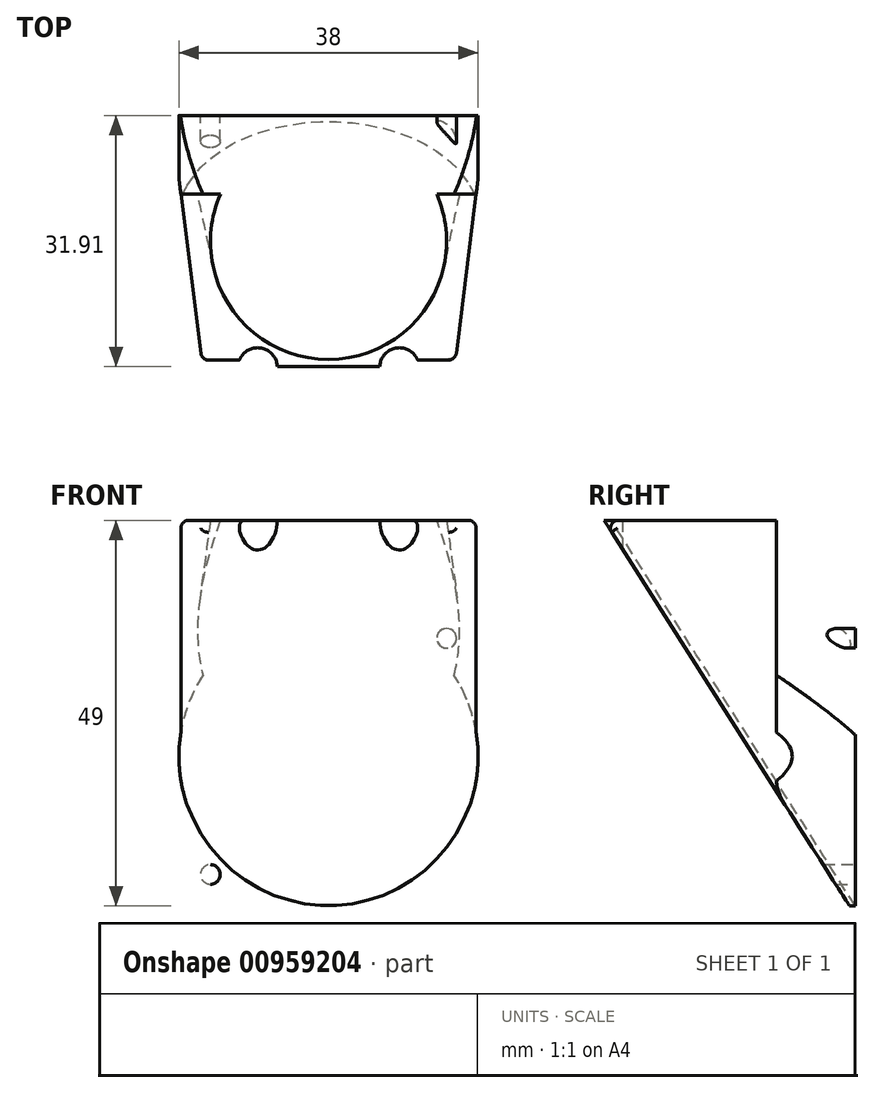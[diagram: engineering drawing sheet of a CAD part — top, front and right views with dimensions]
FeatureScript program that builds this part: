
annotation { "Feature Type Name" : "Feature", "Feature Type Description" : "" }
export const myFeature = defineFeature(function(context is Context, id is Id, definition is map)
    precondition{}
    {
        {
            var Q0;
            Q0=qCreatedBy(makeId("Top.planeOp"),FACE);
            var sketch = newSketch(context, id + "F0", { "sketchPlane" : qUnion([Q0])});
            skLineSegment(sketch, "E0.bottom", {"start": v(16, -16) * mm, "end": v(-16, -16) * mm});
            skPoint(sketch, "E0.middle", {"position": v(0, 0) * mm});
            skLineSegment(sketch, "E1", {"start": v(-20, 20.39) * mm, "end": v(-20, 8.27) * mm, "construction": true});
            skLineSegment(sketch, "E2", {"start": v(20, 19.24) * mm, "end": v(20, 5.53) * mm, "construction": true});
            skLineSegment(sketch, "E3", {"start": v(-16, 16) * mm, "end": v(-20, 16) * mm, "construction": true});
            skLineSegment(sketch, "E4", {"start": v(16, 16) * mm, "end": v(20, 16) * mm, "construction": true});
            skLineSegment(sketch, "E5", {"start": v(-16, -16) * mm, "end": v(-20, 16) * mm});
            skLineSegment(sketch, "E6", {"start": v(16, -16) * mm, "end": v(20, 16) * mm});
            skLineSegment(sketch, "E7", {"start": v(-20, 16) * mm, "end": v(20, 16) * mm});
            skCircle(sketch, "E8", {"center": v(-9, -16) * mm, "radius": 2.5 * mm});
            skCircle(sketch, "E9.MirrorC", {"center": v(9, -16) * mm, "radius": 2.5 * mm});
            skSolve(sketch);
        }
        {
            var Q0;
            Q0=makeQuery(id+"F0.imprint","IMPRINT",FACE,{"disambiguationData":[TD([[makeQuery(id+"F0.imprint","IMPRINT",EDGE,{"derivedFrom":sQuery(id+"F0.wireOp",EDGE,"E0.bottom")}),-1.0]])]});
            var sketch = newSketch(context, id + "F1", { "sketchPlane" : qUnion([Q0])});
            skCircle(sketch, "E10", {"center": v(0, 0) * mm, "radius": 15 * mm});
            skLineSegment(sketch, "E11.bottom", {"start": v(15, -15) * mm, "end": v(-15, -15) * mm, "construction": true});
            skLineSegment(sketch, "E11.top", {"start": v(15, 15) * mm, "end": v(-15, 15) * mm, "construction": true});
            skLineSegment(sketch, "E11.left", {"start": v(15, -15) * mm, "end": v(15, 15) * mm, "construction": true});
            skLineSegment(sketch, "E11.right", {"start": v(-15, -15) * mm, "end": v(-15, 15) * mm, "construction": true});
            skLineSegment(sketch, "E12", {"start": v(-15, 15) * mm, "end": v(15, -15) * mm, "construction": true});
            skLineSegment(sketch, "E13", {"start": v(15, 15) * mm, "end": v(-15, -15) * mm, "construction": true});
            skPoint(sketch, "E14", {"position": v(-10.6, -10.6) * mm});
            skPoint(sketch, "E15", {"position": v(-10.6, 10.6) * mm});
            skPoint(sketch, "E16", {"position": v(10.6, 10.6) * mm});
            skPoint(sketch, "E17", {"position": v(10.6, -10.6) * mm});
            skSolve(sketch);
        }
        {
            var Q0;
            Q0=makeQuery(id+"F0.imprint","IMPRINT",FACE,{"disambiguationData":[TD([[makeQuery(id+"F0.imprint","IMPRINT",EDGE,{"derivedFrom":sQuery(id+"F0.wireOp",EDGE,"E0.bottom")}),-1.0]])]});
            extrude(context, id + "F2", {"entities" : qUnion([Q0]), "oppositeDirection" : true, "depth" : 50 * mm, "offsetDistance" : 25 * mm});
        }
        {
            var Q0;
            Q0=makeQuery(id+"F2.opExtrude","SWEPT_FACE",FACE,{"disambiguationData":[OSD([sQuery(id+"F0.wireOp",EDGE,"E7")])]});
            var sketch = newSketch(context, id + "F3", { "sketchPlane" : qUnion([Q0])});
            skLineSegment(sketch, "E18.bottom", {"start": v(20, -50) * mm, "end": v(-20, -50) * mm});
            skLineSegment(sketch, "E18.top", {"start": v(20, -10) * mm, "end": v(-20, -10) * mm, "construction": true});
            skLineSegment(sketch, "E18.left", {"start": v(20, -50) * mm, "end": v(20, -10) * mm});
            skLineSegment(sketch, "E18.right", {"start": v(-20, -50) * mm, "end": v(-20, -10) * mm});
            skLineSegment(sketch, "E19", {"start": v(20, -10) * mm, "end": v(-20, -50) * mm, "construction": true});
            skLineSegment(sketch, "E20", {"start": v(-20, -10) * mm, "end": v(20, -50) * mm, "construction": true});
            skCircle(sketch, "E21", {"center": v(0, -30) * mm, "radius": 19 * mm});
            skCircle(sketch, "E22", {"center": v(0, -30) * mm, "radius": 21.21 * mm, "construction": true});
            skCircle(sketch, "E23", {"center": v(-15, -45) * mm, "radius": 1.25 * mm});
            skLineSegment(sketch, "E24", {"start": v(-20, -30) * mm, "end": v(20, -30) * mm, "construction": true});
            skCircle(sketch, "E25.MirrorC", {"center": v(-15, -15) * mm, "radius": 1.25 * mm});
            skCircle(sketch, "E26.MirrorC", {"center": v(15, -45) * mm, "radius": 1.25 * mm});
            skCircle(sketch, "E27.MirrorC", {"center": v(15, -15) * mm, "radius": 1.25 * mm});
            skPoint(sketch, "E28", {"position": v(-13.44, -16.56) * mm});
            skPoint(sketch, "E29", {"position": v(-13.44, -43.44) * mm});
            skPoint(sketch, "E30", {"position": v(13.44, -43.44) * mm});
            skPoint(sketch, "E31", {"position": v(13.44, -16.56) * mm});
            skSolve(sketch);
        }
        {
            var Q1;
            Q1=makeQuery(id+"F1.imprint","IMPRINT",FACE,{"disambiguationData":[TD([[makeQuery(id+"F1.imprint","IMPRINT",EDGE,{"derivedFrom":sQuery(id+"F1.wireOp",EDGE,"E10")}),1.0]])]});
            var Q2;
            Q2=makeQuery(id+"F3.imprint","IMPRINT",FACE,{"disambiguationData":[TD([[makeQuery(id+"F3.imprint","IMPRINT",EDGE,{"derivedFrom":sQuery(id+"F3.wireOp",EDGE,"E21")}),1.0]])]});
            var Q3;
            Q3=makeQuery(id+"F3.imprint","IMPRINT",FACE,{"disambiguationData":[TD([[makeQuery(id+"F3.imprint","IMPRINT",EDGE,{"derivedFrom":sQuery(id+"F3.wireOp",EDGE,"E21")}),1.0]])]});
            var Q4;
            Q4=makeQuery(id+"F1.imprint","IMPRINT",FACE,{"disambiguationData":[TD([[makeQuery(id+"F1.imprint","IMPRINT",EDGE,{"derivedFrom":sQuery(id+"F1.wireOp",EDGE,"E10")}),1.0]])]});
            var Q5;
            Q5=sQuery(id+"F1.wireOp",VERTEX,"E15");
            var Q6;
            Q6=sQuery(id+"F3.wireOp",VERTEX,"E31");
            loft(context, id + "F4", {"operationType" : NewBodyOperationType.REMOVE, "sheetProfilesArray" : [{ "sheetProfileEntities" : qUnion([Q1]) }, { "sheetProfileEntities" : qUnion([Q2]) }], "wireProfilesArray" : [{ "wireProfileEntities" : qUnion([Q3]) }, { "wireProfileEntities" : qUnion([Q4]) }], "matchConnections" : true, "connections" : [{ "connectionEntities" : qUnion([Q5, Q6]), "connectionEdgeQueries" : qUnion([]), "connectionEdgeParameters" : [] }]});
        }
        {
            var Q0;
            Q0=makeQuery(id+"F2.opExtrude","SWEPT_EDGE",EDGE,{"disambiguationData":[OSD([sQuery(id+"F0.wireOp",EDGE,"E6"),sQuery(id+"F0.wireOp",EDGE,"E7")])]});
            cPlane(context, id + "F5", {"entities" : qUnion([Q0]), "cplaneType" : CPlaneType.LINE_ANGLE, "offset" : 25 * mm, "angle" : 0 * degree, "oppositeDirection" : true, "width" : 150 * mm, "height" : 150 * mm});
        }
        {
            var Q0;
            Q0=qCreatedBy(id+"F5.planeOp",FACE);
            var sketch = newSketch(context, id + "F6", { "sketchPlane" : qUnion([Q0])});
            skLineSegment(sketch, "E32", {"start": v(-15.9, 0) * mm, "end": v(16.05, -50.24) * mm});
            skLineSegment(sketch, "E33", {"start": v(16.05, -50.24) * mm, "end": v(-19.34, -50.24) * mm});
            skLineSegment(sketch, "E34", {"start": v(-19.34, -50.24) * mm, "end": v(-19.34, 0) * mm});
            skLineSegment(sketch, "E35", {"start": v(-19.34, 0) * mm, "end": v(-15.9, 0) * mm});
            skSolve(sketch);
        }
        {
            var Q0;
            Q0=makeQuery(id+"F6.imprint","IMPRINT",FACE,{"disambiguationData":[TD([[makeQuery(id+"F6.imprint","IMPRINT",EDGE,{"derivedFrom":sQuery(id+"F6.wireOp",EDGE,"E32")}),-1.0]])]});
            extrude(context, id + "F7", {"entities" : qUnion([Q0]), "operationType" : NewBodyOperationType.REMOVE, "oppositeDirection" : true, "depth" : 40 * mm, "offsetDistance" : 25 * mm});
        }
        {
            var Q0;
            Q0=makeQuery(id+"F3.imprint","IMPRINT",FACE,{"disambiguationData":[TD([[makeQuery(id+"F3.imprint","IMPRINT",EDGE,{"derivedFrom":sQuery(id+"F3.wireOp",EDGE,"E23")}),1.0]])]});
            var Q1;
            Q1=makeQuery(id+"F3.imprint","IMPRINT",FACE,{"disambiguationData":[TD([[makeQuery(id+"F3.imprint","IMPRINT",EDGE,{"derivedFrom":sQuery(id+"F3.wireOp",EDGE,"E25.MirrorC")}),-1.0]])]});
            var Q2;
            Q2=makeQuery(id+"F3.imprint","IMPRINT",FACE,{"disambiguationData":[TD([[makeQuery(id+"F3.imprint","IMPRINT",EDGE,{"derivedFrom":sQuery(id+"F3.wireOp",EDGE,"E27.MirrorC")}),1.0]])]});
            var Q3;
            Q3=makeQuery(id+"F3.imprint","IMPRINT",FACE,{"disambiguationData":[TD([[makeQuery(id+"F3.imprint","IMPRINT",EDGE,{"derivedFrom":sQuery(id+"F3.wireOp",EDGE,"E26.MirrorC")}),-1.0]])]});
            extrude(context, id + "F8", {"entities" : qUnion([Q0, Q1, Q2, Q3]), "operationType" : NewBodyOperationType.REMOVE, "oppositeDirection" : true, "depth" : 10 * mm, "offsetDistance" : 25 * mm});
        }
        {
            var Q0;
            Q0=makeQuery(id+"F2.opExtrude","SWEPT_EDGE",EDGE,{"disambiguationData":[OSD([sQuery(id+"F0.wireOp",EDGE,"E6"),sQuery(id+"F0.wireOp",EDGE,"E7")])]});
            var Q1;
            Q1=makeQuery(id+"F2.opExtrude","SWEPT_EDGE",EDGE,{"disambiguationData":[OSD([sQuery(id+"F0.wireOp",EDGE,"E5"),sQuery(id+"F0.wireOp",EDGE,"E7")])]});
            var Q2;
            Q2=makeQuery(id+"F2.opExtrude","CAP_EDGE",EDGE,{"disambiguationData":[OSD([sQuery(id+"F0.wireOp",EDGE,"E7")])],"isStart":false});
            var Q3;
            Q3=makeQuery(id+"F7.boolean.opBoolean","INTERSECT",EDGE,{"derivedFrom":[makeQuery(id+"F2.opExtrude","SWEPT_FACE",FACE,{"disambiguationData":[OSD([sQuery(id+"F0.wireOp",EDGE,"E6")])]}),makeQuery(id+"F7.opExtrude","SWEPT_FACE",FACE,{"disambiguationData":[OSD([sQuery(id+"F6.wireOp",EDGE,"E32")])]})]});
            var Q4;
            Q4=makeQuery(id+"F7.boolean.opBoolean","INTERSECT",EDGE,{"derivedFrom":[makeQuery(id+"F2.opExtrude","SWEPT_FACE",FACE,{"disambiguationData":[OSD([sQuery(id+"F0.wireOp",EDGE,"E5")])]}),makeQuery(id+"F7.opExtrude","SWEPT_FACE",FACE,{"disambiguationData":[OSD([sQuery(id+"F6.wireOp",EDGE,"E32")])]})]});
            fillet(context, id + "F9", {"entities" : qUnion([Q0, Q1, Q2, Q3, Q4]), "radius" : 1 * mm, "tangentPropagation" : true, "allowEdgeOverflow" : false});
        }
        {
            var Q0;
            Q0=makeQuery(id+"F2.opExtrude","CAP_EDGE",EDGE,{"disambiguationData":[OSD([sQuery(id+"F0.wireOp",EDGE,"E6")])],"isStart":true});
            var Q1;
            Q1=makeQuery(id+"F2.opExtrude","CAP_EDGE",EDGE,{"disambiguationData":[OSD([sQuery(id+"F0.wireOp",EDGE,"E5")])],"isStart":true});
            fillet(context, id + "F10", {"entities" : qUnion([Q0, Q1]), "radius" : 1 * mm, "tangentPropagation" : true, "allowEdgeOverflow" : false});
        }
    });
